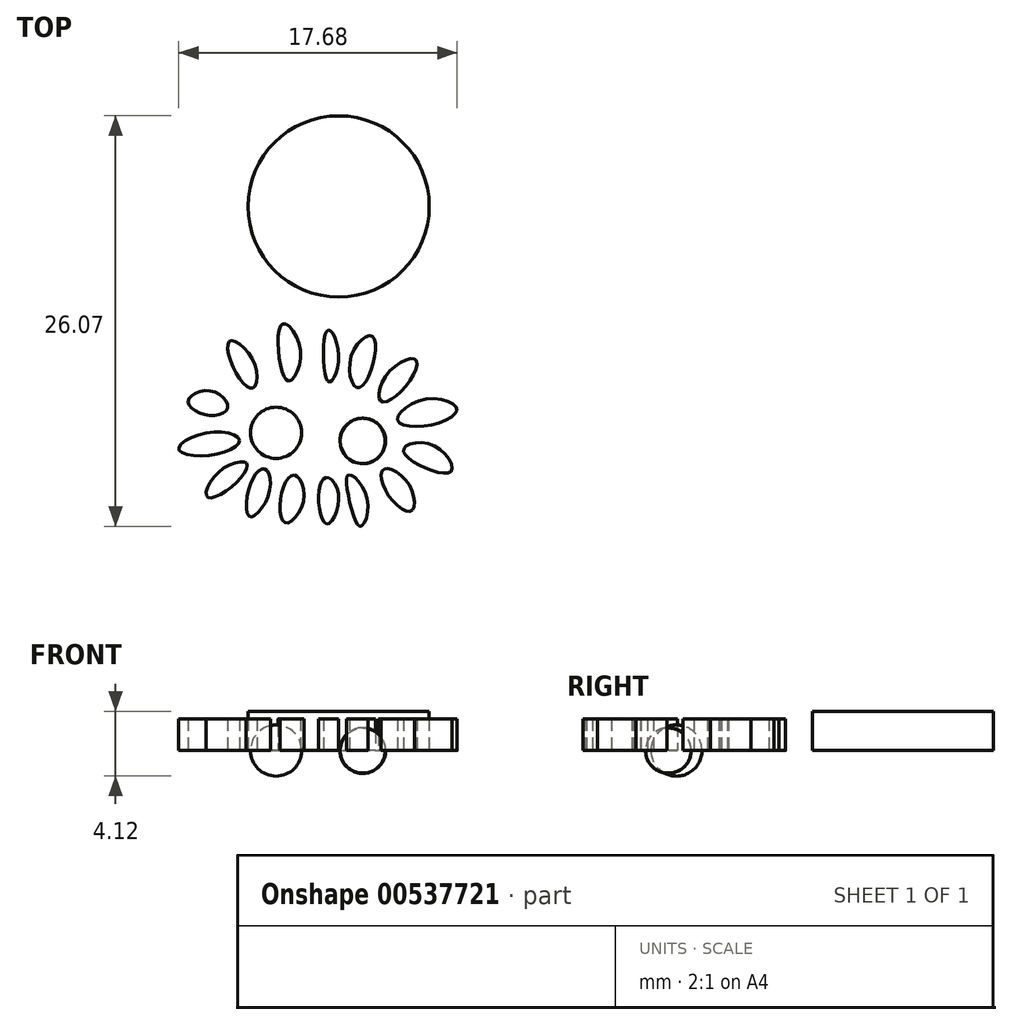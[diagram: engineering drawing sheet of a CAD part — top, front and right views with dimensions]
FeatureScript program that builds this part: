
annotation { "Feature Type Name" : "Feature", "Feature Type Description" : "" }
export const myFeature = defineFeature(function(context is Context, id is Id, definition is map)
    precondition{}
    {
        {
            var Q0;
            Q0=qCreatedBy(makeId("Top.planeOp"),FACE);
            var sketch = newSketch(context, id + "F0", { "sketchPlane" : qUnion([Q0])});
            skLineSegment(sketch, "E0", {"start": v(0, 0) * mm, "end": v(0, -41.3) * mm});
            skSolve(sketch);
        }
        {
            var Q0;
            Q0=qCreatedBy(makeId("Top.planeOp"),FACE);
            var sketch = newSketch(context, id + "F1", { "sketchPlane" : qUnion([Q0])});
            skArc(sketch, "E1", {"start": v(0, 0) * mm, "mid": v(-20.89, -20.6) * mm, "end": v(0, -41.18) * mm});
            skSolve(sketch);
        }
        {
            var Q0;
            Q0=sQuery(id+"F1.wireOp",EDGE,"E1");
            var Q1;
            Q1=sQuery(id+"F0.wireOp",EDGE,"E0");
            revolve(context, id + "F2", {"bodyType" : ToolBodyType.SURFACE, "surfaceEntities" : qUnion([Q0]), "axis" : qUnion([Q1]), "revolveType" : RevolveType.ONE_DIRECTION, "angle" : 180 * degree});
        }
        {
            var Q0;
            Q0=qCreatedBy(makeId("Top.planeOp"),FACE);
            var sketch = newSketch(context, id + "F3", { "sketchPlane" : qUnion([Q0])});
            skCircle(sketch, "E2", {"center": v(0, -20.03) * mm, "radius": 5.75 * mm});
            skSolve(sketch);
        }
        {
            var Q0;
            Q0=makeQuery(id+"F3.imprint","IMPRINT",FACE,{"disambiguationData":[TD([[makeQuery(id+"F3.imprint","IMPRINT",EDGE,{"derivedFrom":sQuery(id+"F3.wireOp",EDGE,"E2")}),1.0]])]});
            extrude(context, id + "F4", {"entities" : qUnion([Q0]), "depth" : 2.5 * mm, "offsetDistance" : 25 * mm});
        }
        {
            var Q0;
            Q0=makeQuery(id+"F4.opExtrude","CAP_FACE",FACE,{"disambiguationData":[OSD([sQuery(id+"F3.wireOp",EDGE,"E2")])],"isStart":false});
            var sketch = newSketch(context, id + "F5", { "sketchPlane" : qUnion([Q0])});
            skFitSpline(sketch, "E3", {"points": [v(4, -23.03) * mm, v(1.35, -24.93) * mm, v(-1.91, -24.7) * mm, v(-4.46, -23.66) * mm, v(-2.2, -23.63) * mm, v(0, -24.32) * mm, v(2.26, -23.2) * mm, v(4.34, -21.97) * mm, v(3.73, -20.23) * mm, v(4.67, -18.4) * mm, v(1.83, -15.21) * mm, v(2.96, -18.87) * mm, v(2.97, -21.66) * mm, v(0, -23.22) * mm, v(-4.25, -22.04) * mm, v(-3.59, -16.9) * mm, v(0, -15.2) * mm, v(-3.33, -20.37) * mm, v(-1.67, -21.88) * mm, v(1.4, -21.45) * mm, v(1.07, -18.52) * mm, v(1.52, -17.33) * mm], "startDerivative": vector(-52.12, -48.65) * mm, "endDerivative": vector(23.32, 31.06) * mm});
            skSolve(sketch);
        }
        {
            var Q0;
            Q0=sQuery(id+"F5.wireOp",EDGE,"E3");
            extrude(context, id + "F6", {"bodyType" : ToolBodyType.SURFACE, "surfaceEntities" : qUnion([Q0]), "depth" : 1 * mm, "offsetDistance" : 25 * mm});
        }
        {
            var Q0;
            Q0=qCreatedBy(makeId("Top.planeOp"),FACE);
            var sketch = newSketch(context, id + "F7", { "sketchPlane" : qUnion([Q0])});
            skLineSegment(sketch, "E4", {"start": v(-3.98, -36.03) * mm, "end": v(-3.98, -32.78) * mm});
            skArc(sketch, "E5", {"start": v(-3.98, -36.03) * mm, "mid": v(-2.35, -34.4) * mm, "end": v(-3.98, -32.78) * mm});
            skSolve(sketch);
        }
        {
            var Q0;
            Q0=makeQuery(id+"F7.imprint","IMPRINT",FACE,{"disambiguationData":[TD([[makeQuery(id+"F7.imprint","IMPRINT",EDGE,{"derivedFrom":sQuery(id+"F7.wireOp",EDGE,"E4")}),-1.0]])]});
            var Q1;
            Q1=sQuery(id+"F7.wireOp",EDGE,"E4");
            revolve(context, id + "F8", {"entities" : qUnion([Q0]), "axis" : qUnion([Q1]), "revolveType" : RevolveType.FULL});
        }
        {
            var Q0;
            Q0=qCreatedBy(makeId("Top.planeOp"),FACE);
            var sketch = newSketch(context, id + "F9", { "sketchPlane" : qUnion([Q0])});
            skLineSegment(sketch, "E6", {"start": v(0.66, -33.22) * mm, "end": v(0.66, -35.78) * mm});
            skArc(sketch, "E7", {"start": v(0.66, -33.22) * mm, "mid": v(-0.63, -34.5) * mm, "end": v(0.66, -35.78) * mm});
            skSolve(sketch);
        }
        {
            var Q0;
            Q0=makeQuery(id+"F9.imprint","IMPRINT",FACE,{"disambiguationData":[TD([[makeQuery(id+"F9.imprint","IMPRINT",EDGE,{"derivedFrom":sQuery(id+"F9.wireOp",EDGE,"E6")}),-1.0]])]});
            var Q1;
            Q1=sQuery(id+"F9.wireOp",EDGE,"E6");
            revolve(context, id + "F10", {"entities" : qUnion([Q0]), "axis" : qUnion([Q1]), "revolveType" : RevolveType.FULL});
        }
        {
            var Q0;
            Q0=makeQuery(id+"F10.opRevolve","SWEPT_BODY",BODY,{"disambiguationData":[OSD([sQuery(id+"F9.wireOp",EDGE,"E6"),sQuery(id+"F9.wireOp",EDGE,"E7")])]});
            deleteBodies(context, id + "F11", {"entities" : qUnion([Q0])});
        }
        {
            var Q0;
            Q0=qCreatedBy(makeId("Top.planeOp"),FACE);
            var sketch = newSketch(context, id + "F12", { "sketchPlane" : qUnion([Q0])});
            skLineSegment(sketch, "E8", {"start": v(1.53, -33.48) * mm, "end": v(1.53, -36.36) * mm});
            skArc(sketch, "E9", {"start": v(1.53, -33.48) * mm, "mid": v(0.08, -34.92) * mm, "end": v(1.53, -36.36) * mm});
            skSolve(sketch);
        }
        {
            var Q0;
            Q0=makeQuery(id+"F12.imprint","IMPRINT",FACE,{"disambiguationData":[TD([[makeQuery(id+"F12.imprint","IMPRINT",EDGE,{"derivedFrom":sQuery(id+"F12.wireOp",EDGE,"E8")}),-1.0]])]});
            var Q1;
            Q1=sQuery(id+"F12.wireOp",EDGE,"E8");
            revolve(context, id + "F13", {"entities" : qUnion([Q0]), "axis" : qUnion([Q1]), "revolveType" : RevolveType.FULL});
        }
        {
            var Q0;
            Q0=qCreatedBy(makeId("Top.planeOp"),FACE);
            var sketch = newSketch(context, id + "F14", { "sketchPlane" : qUnion([Q0])});
            skFitSpline(sketch, "E10", {"points": [v(-5.44, -31.57) * mm, v(-6.63, -30.4) * mm, v(-6.91, -28.57) * mm, v(-5.42, -29.84) * mm, v(-5.44, -31.57) * mm]});
            skFitSpline(sketch, "E11", {"points": [v(-3.77, -29.65) * mm, v(-3.14, -31.1) * mm, v(-2.42, -29.13) * mm, v(-3.54, -27.49) * mm, v(-3.77, -29.65) * mm]});
            skFitSpline(sketch, "E12", {"points": [v(-7.07, -32.83) * mm, v(-8.36, -33.28) * mm, v(-9.56, -32.38) * mm, v(-8.06, -31.75) * mm, v(-7.07, -32.83) * mm]});
            skFitSpline(sketch, "E13", {"points": [v(-6.3, -34.88) * mm, v(-8.21, -34.38) * mm, v(-10.16, -35.44) * mm, v(-7.98, -35.8) * mm, v(-6.3, -34.88) * mm]});
            skFitSpline(sketch, "E14", {"points": [v(-5.86, -36.33) * mm, v(-7.57, -36.86) * mm, v(-8.35, -38.47) * mm, v(-6.62, -37.7) * mm, v(-5.86, -36.33) * mm]});
            skFitSpline(sketch, "E15", {"points": [v(-4.7, -36.7) * mm, v(-5.63, -37.7) * mm, v(-5.65, -39.73) * mm, v(-4.42, -38.24) * mm, v(-4.7, -36.7) * mm]});
            skFitSpline(sketch, "E16", {"points": [v(-2.82, -37.1) * mm, v(-3.66, -38.41) * mm, v(-3.35, -40.12) * mm, v(-2.2, -38.62) * mm, v(-2.82, -37.1) * mm]});
            skFitSpline(sketch, "E17", {"points": [v(-0.8, -37.25) * mm, v(-1.28, -38.6) * mm, v(-0.72, -40.19) * mm, v(0, -38.37) * mm, v(-0.8, -37.25) * mm]});
            skFitSpline(sketch, "E18", {"points": [v(0.64, -37.07) * mm, v(0.6, -38.32) * mm, v(1.38, -40.34) * mm, v(1.8, -38.55) * mm, v(0.64, -37.07) * mm]});
            skFitSpline(sketch, "E19", {"points": [v(2.9, -36.7) * mm, v(3, -38.1) * mm, v(4.58, -39.39) * mm, v(4.47, -37.7) * mm, v(2.9, -36.7) * mm]});
            skFitSpline(sketch, "E20", {"points": [v(4.14, -35.42) * mm, v(5.18, -36.49) * mm, v(7.16, -36.82) * mm, v(6, -35.19) * mm, v(4.14, -35.42) * mm]});
            skFitSpline(sketch, "E21", {"points": [v(3.73, -33.59) * mm, v(5.74, -33.93) * mm, v(7.51, -32.9) * mm, v(5.5, -32.28) * mm, v(3.73, -33.59) * mm]});
            skFitSpline(sketch, "E22", {"points": [v(2.65, -32.37) * mm, v(4.05, -31.7) * mm, v(4.9, -29.77) * mm, v(3.2, -30.54) * mm, v(2.65, -32.37) * mm]});
            skFitSpline(sketch, "E23", {"points": [v(1.14, -31.54) * mm, v(2.1, -30.33) * mm, v(2.1, -28.25) * mm, v(0.8, -29.53) * mm, v(1.14, -31.54) * mm]});
            skFitSpline(sketch, "E24", {"points": [v(-0.7, -31.12) * mm, v(0, -29.63) * mm, v(-0.73, -27.92) * mm, v(-0.7, -31.12) * mm]});
            skSolve(sketch);
        }
        {
            var Q0;
            Q0 = qSketchRegion(id + "F14", true);
            extrude(context, id + "F15", {"entities" : qUnion([Q0]), "depth" : 2 * mm, "offsetDistance" : 25 * mm});
        }
    });
